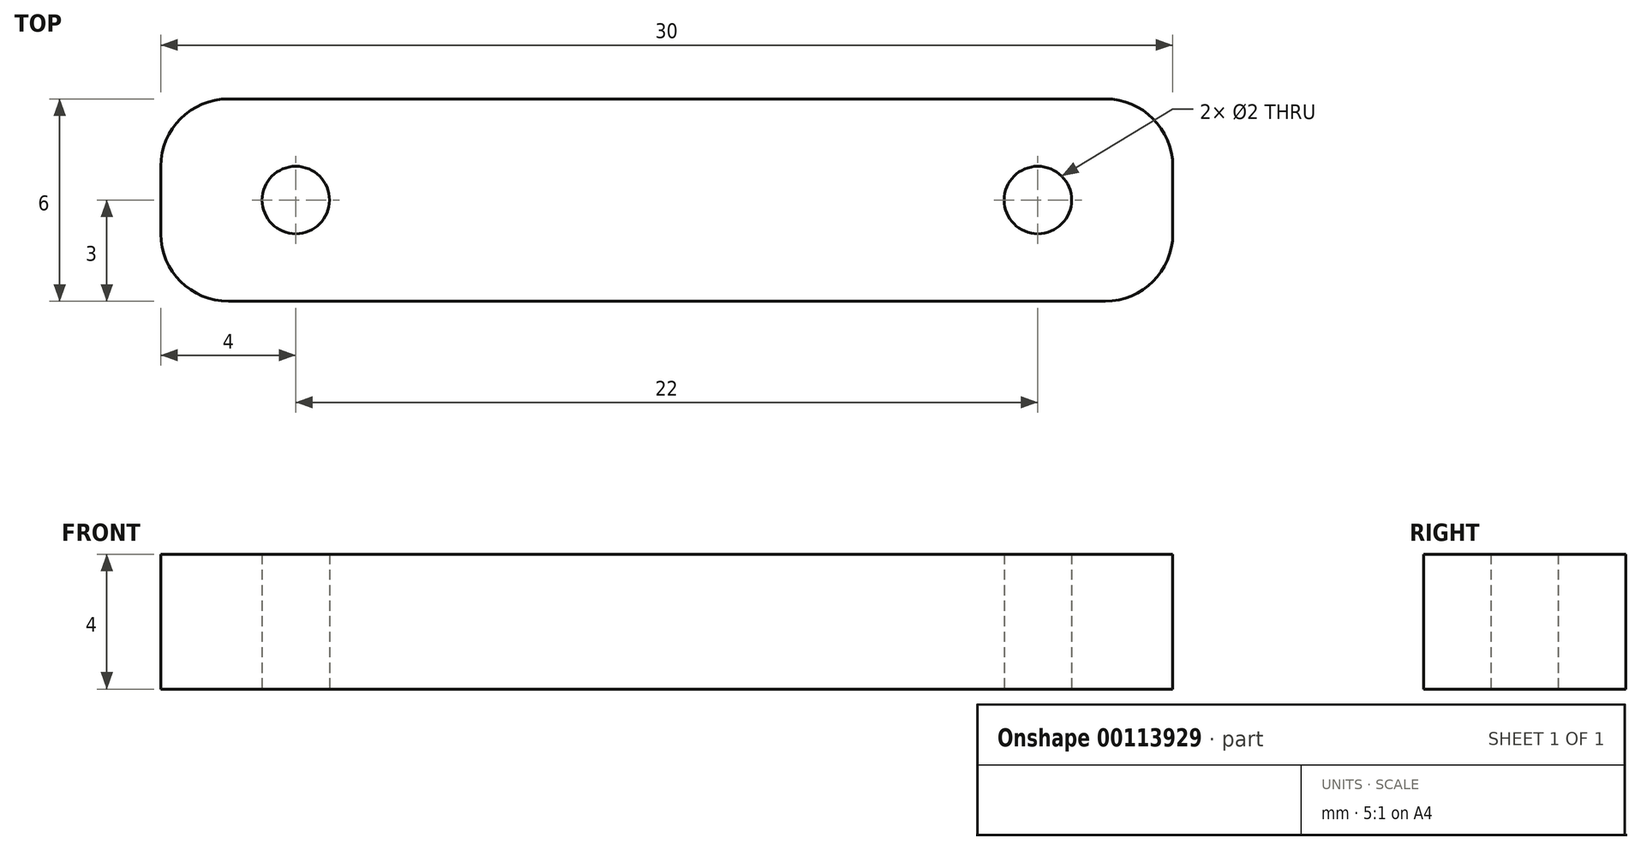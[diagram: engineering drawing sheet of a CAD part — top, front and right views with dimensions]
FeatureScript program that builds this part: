
annotation { "Feature Type Name" : "Feature", "Feature Type Description" : "" }
export const myFeature = defineFeature(function(context is Context, id is Id, definition is map)
    precondition{}
    {
        {
            var Q0;
            Q0=qCreatedBy(makeId("Top.planeOp"),FACE);
            var sketch = newSketch(context, id + "F0", { "sketchPlane" : qUnion([Q0])});
            skLineSegment(sketch, "E0.bottom", {"start": v(-15, 3) * mm, "end": v(15, 3) * mm});
            skLineSegment(sketch, "E0.top", {"start": v(-15, -3) * mm, "end": v(15, -3) * mm});
            skLineSegment(sketch, "E0.left", {"start": v(-15, 3) * mm, "end": v(-15, -3) * mm});
            skLineSegment(sketch, "E0.right", {"start": v(15, 3) * mm, "end": v(15, -3) * mm});
            skPoint(sketch, "E0.middle", {"position": v(0, 0) * mm});
            skLineSegment(sketch, "E1", {"start": v(0, 0) * mm, "end": v(-11, 0) * mm});
            skLineSegment(sketch, "E2", {"start": v(0, 0) * mm, "end": v(11, 0) * mm});
            skSolve(sketch);
        }
        {
            var Q0;
            Q0=makeQuery(id+"F0.imprint","IMPRINT",FACE,{"disambiguationData":[TD([[makeQuery(id+"F0.imprint","IMPRINT",EDGE,{"derivedFrom":sQuery(id+"F0.wireOp",EDGE,"E0.bottom")}),-1.0]])]});
            extrude(context, id + "F1", {"entities" : qUnion([Q0]), "depth" : 4 * mm});
        }
        {
            var Q0;
            Q0=makeQuery(id+"F1.opExtrude","SWEPT_EDGE",EDGE,{"disambiguationData":[OSD([sQuery(id+"F0.wireOp",EDGE,"E0.bottom"),sQuery(id+"F0.wireOp",EDGE,"E0.right")])]});
            var Q1;
            Q1=makeQuery(id+"F1.opExtrude","SWEPT_EDGE",EDGE,{"disambiguationData":[OSD([sQuery(id+"F0.wireOp",EDGE,"E0.top"),sQuery(id+"F0.wireOp",EDGE,"E0.right")])]});
            var Q2;
            Q2=makeQuery(id+"F1.opExtrude","SWEPT_EDGE",EDGE,{"disambiguationData":[OSD([sQuery(id+"F0.wireOp",EDGE,"E0.bottom"),sQuery(id+"F0.wireOp",EDGE,"E0.left")])]});
            var Q3;
            Q3=makeQuery(id+"F1.opExtrude","SWEPT_EDGE",EDGE,{"disambiguationData":[OSD([sQuery(id+"F0.wireOp",EDGE,"E0.top"),sQuery(id+"F0.wireOp",EDGE,"E0.left")])]});
            fillet(context, id + "F2", {"entities" : qUnion([Q0, Q1, Q2, Q3]), "radius" : 2 * mm, "tangentPropagation" : true, "allowEdgeOverflow" : false});
        }
        {
            var Q0;
            Q0=sQuery(id+"F0.wireOp",VERTEX,"E1.end");
            var Q1;
            Q1=sQuery(id+"F0.wireOp",VERTEX,"E2.end");
            var Q2;
            Q2=makeQuery(id+"F1.opExtrude","SWEPT_BODY",BODY,{"disambiguationData":[OSD([sQuery(id+"F0.wireOp",EDGE,"E0.bottom"),sQuery(id+"F0.wireOp",EDGE,"E0.top"),sQuery(id+"F0.wireOp",EDGE,"E0.left"),sQuery(id+"F0.wireOp",EDGE,"E0.right")])]});
            hole(context, id + "F3", {"style" : HoleStyle.SIMPLE, "endStyle" : HoleEndStyle.BLIND, "oppositeDirection" : true, "holeDiameter" : 2 * mm, "holeDepth" : 4 * mm, "locations" : qUnion([Q0, Q1]), "scope" : qUnion([Q2])});
        }
    });
